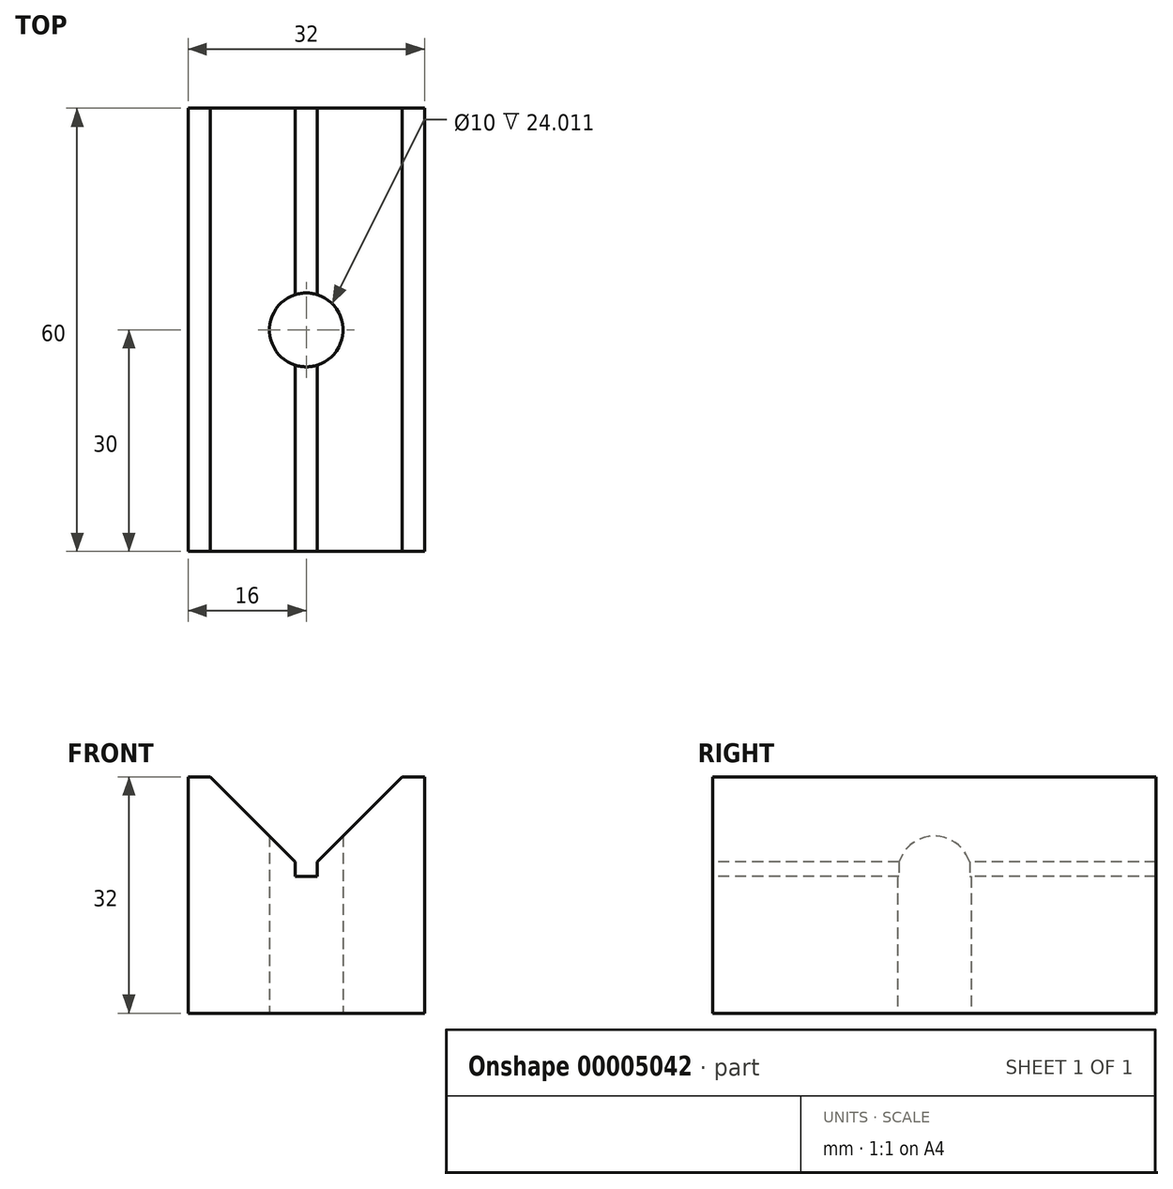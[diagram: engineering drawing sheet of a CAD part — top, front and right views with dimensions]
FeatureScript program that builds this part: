
annotation { "Feature Type Name" : "Feature", "Feature Type Description" : "" }
export const myFeature = defineFeature(function(context is Context, id is Id, definition is map)
    precondition{}
    {
        {
            var Q0;
            Q0=qCreatedBy(makeId("Top.planeOp"),FACE);
            var sketch = newSketch(context, id + "F0", { "sketchPlane" : qUnion([Q0])});
            skLineSegment(sketch, "E0.rect.bottom", {"start": v(16, 30) * mm, "end": v(-16, 30) * mm});
            skLineSegment(sketch, "E0.rect.top", {"start": v(16, -30) * mm, "end": v(-16, -30) * mm});
            skLineSegment(sketch, "E0.rect.left", {"start": v(16, 30) * mm, "end": v(16, -30) * mm});
            skLineSegment(sketch, "E0.rect.right", {"start": v(-16, 30) * mm, "end": v(-16, -30) * mm});
            skPoint(sketch, "E0.rect.middle", {"position": v(0, 0) * mm});
            skCircle(sketch, "E1", {"center": v(0, 0) * mm, "radius": 5 * mm});
            skSolve(sketch);
        }
        {
            var Q0;
            Q0 = qSketchRegion(id + "F0", true);
            extrude(context, id + "F1", {"entities" : qUnion([Q0]), "depth" : 32 * mm});
        }
        {
            var Q0;
            Q0=makeQuery(id+"F1.opExtrude","SWEPT_FACE",FACE,{"disambiguationData":[OSD([sQuery(id+"F0.wireOp",EDGE,"E0.rect.top")])]});
            var sketch = newSketch(context, id + "F2", { "sketchPlane" : qUnion([Q0])});
            skPoint(sketch, "E2", {"position": v(-13, 32) * mm});
            skPoint(sketch, "E3", {"position": v(13, 32) * mm});
            skLineSegment(sketch, "E4", {"start": v(-1.5, 20.5) * mm, "end": v(-1.5, 18.5) * mm});
            skLineSegment(sketch, "E5", {"start": v(-1.5, 18.5) * mm, "end": v(1.5, 18.5) * mm});
            skLineSegment(sketch, "E6", {"start": v(1.5, 18.5) * mm, "end": v(1.5, 20.5) * mm});
            skLineSegment(sketch, "E7", {"start": v(-13, 32) * mm, "end": v(-1.5, 20.5) * mm});
            skLineSegment(sketch, "E8", {"start": v(1.5, 20.5) * mm, "end": v(13, 32) * mm});
            skSolve(sketch);
        }
        {
            var Q0;
            Q0 = qSketchRegion(id + "F2", true);
            var Q1;
            Q1=makeQuery(id+"F2.imprint","IMPRINT",FACE,{"disambiguationData":[TD([[makeQuery(id+"F2.imprint","IMPRINT",EDGE,{"derivedFrom":sQuery(id+"F2.wireOp",EDGE,"E4")}),1.0]])]});
            extrude(context, id + "F3", {"entities" : qUnion([Q0, Q1]), "operationType" : NewBodyOperationType.REMOVE, "oppositeDirection" : true, "depth" : 100 * mm});
        }
    });
